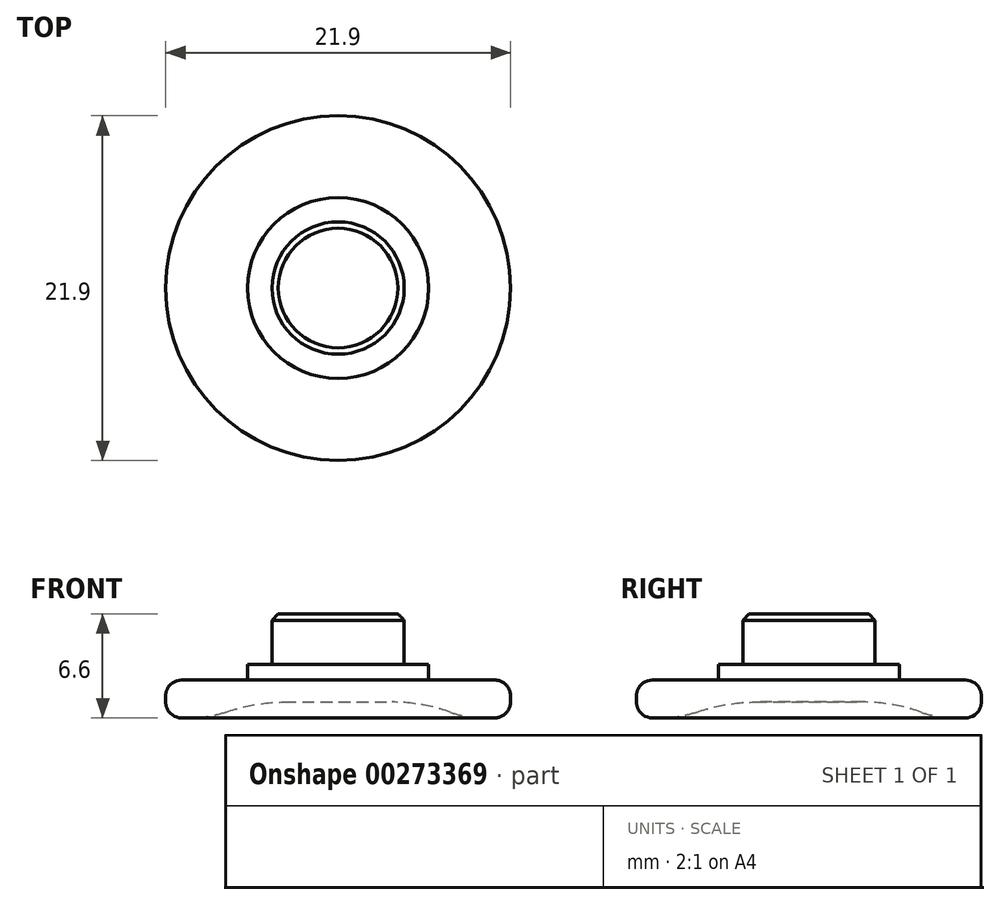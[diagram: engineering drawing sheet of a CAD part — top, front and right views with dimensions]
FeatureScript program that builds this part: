
annotation { "Feature Type Name" : "Feature", "Feature Type Description" : "" }
export const myFeature = defineFeature(function(context is Context, id is Id, definition is map)
    precondition{}
    {
        {
            var Q0;
            Q0=qCreatedBy(makeId("Top.planeOp"),FACE);
            var sketch = newSketch(context, id + "F0", { "sketchPlane" : qUnion([Q0])});
            skCircle(sketch, "E0", {"center": v(0, 0) * mm, "radius": 10.95 * mm});
            skSolve(sketch);
        }
        {
            var Q0;
            Q0=makeQuery(id+"F0.imprint","IMPRINT",FACE,{"disambiguationData":[TD([[makeQuery(id+"F0.imprint","IMPRINT",EDGE,{"derivedFrom":sQuery(id+"F0.wireOp",EDGE,"E0")}),1.0]])]});
            extrude(context, id + "F1", {"entities" : qUnion([Q0]), "depth" : 2.4 * mm});
        }
        {
            var Q0;
            Q0=makeQuery(id+"F1.opExtrude","CAP_FACE",FACE,{"disambiguationData":[OSD([sQuery(id+"F0.wireOp",EDGE,"E0")])],"isStart":false});
            var sketch = newSketch(context, id + "F2", { "sketchPlane" : qUnion([Q0])});
            skCircle(sketch, "E1", {"center": v(0, 0) * mm, "radius": 4.2 * mm});
            skSolve(sketch);
        }
        {
            var Q0;
            Q0=makeQuery(id+"F2.imprint","IMPRINT",FACE,{"disambiguationData":[TD([[makeQuery(id+"F2.imprint","IMPRINT",EDGE,{"derivedFrom":sQuery(id+"F2.wireOp",EDGE,"E1")}),1.0]])]});
            extrude(context, id + "F3", {"entities" : qUnion([Q0]), "operationType" : NewBodyOperationType.ADD, "depth" : 4.2 * mm});
        }
        {
            var Q0;
            Q0=makeQuery(id+"F1.opExtrude","CAP_EDGE",EDGE,{"disambiguationData":[OSD([sQuery(id+"F0.wireOp",EDGE,"E0")])],"isStart":false});
            fillet(context, id + "F4", {"entities" : qUnion([Q0]), "radius" : 1 * mm, "tangentPropagation" : true, "allowEdgeOverflow" : false});
        }
        {
            var Q0;
            Q0=makeQuery(id+"F1.opExtrude","CAP_FACE",FACE,{"disambiguationData":[OSD([sQuery(id+"F0.wireOp",EDGE,"E0")])],"isStart":false});
            var sketch = newSketch(context, id + "F5", { "sketchPlane" : qUnion([Q0])});
            skCircle(sketch, "E2", {"center": v(0, 0) * mm, "radius": 5.75 * mm});
            skSolve(sketch);
        }
        {
            var Q0;
            Q0=makeQuery(id+"F5.imprint","IMPRINT",FACE,{"disambiguationData":[TD([[makeQuery(id+"F5.imprint","IMPRINT",EDGE,{"derivedFrom":sQuery(id+"F5.wireOp",EDGE,"E2")}),1.0]])]});
            extrude(context, id + "F6", {"entities" : qUnion([Q0]), "operationType" : NewBodyOperationType.ADD, "depth" : 1 * mm});
        }
        {
            var Q0;
            Q0=makeQuery(id+"F1.opExtrude","CAP_EDGE",EDGE,{"disambiguationData":[OSD([sQuery(id+"F0.wireOp",EDGE,"E0")])],"isStart":true});
            fillet(context, id + "F7", {"entities" : qUnion([Q0]), "radius" : 1 * mm, "tangentPropagation" : true, "allowEdgeOverflow" : false});
        }
        {
            var Q0;
            Q0=makeQuery(id+"F1.opExtrude","CAP_FACE",FACE,{"disambiguationData":[OSD([sQuery(id+"F0.wireOp",EDGE,"E0")])],"isStart":true});
            var sketch = newSketch(context, id + "F8", { "sketchPlane" : qUnion([Q0])});
            skCircle(sketch, "E3", {"center": v(0, 0) * mm, "radius": 8 * mm});
            skSolve(sketch);
        }
        {
            var Q0;
            Q0=makeQuery(id+"F8.imprint","IMPRINT",FACE,{"disambiguationData":[TD([[makeQuery(id+"F8.imprint","IMPRINT",EDGE,{"derivedFrom":sQuery(id+"F8.wireOp",EDGE,"E3")}),1.0]])]});
            extrude(context, id + "F9", {"entities" : qUnion([Q0]), "operationType" : NewBodyOperationType.REMOVE, "oppositeDirection" : true, "depth" : 1 * mm});
        }
        {
            var Q0;
            Q0=makeQuery(id+"F9.boolean.opBoolean","COPY",EDGE,{"derivedFrom":makeQuery(id+"F9.opExtrude","CAP_EDGE",EDGE,{"disambiguationData":[OSD([sQuery(id+"F8.wireOp",EDGE,"E3")])],"isStart":false})});
            fillet(context, id + "F10", {"entities" : qUnion([Q0]), "radius" : 11 * mm, "tangentPropagation" : true, "allowEdgeOverflow" : false});
        }
        {
            var Q0;
            Q0=makeQuery(id+"F3.opExtrude","CAP_EDGE",EDGE,{"disambiguationData":[OSD([sQuery(id+"F2.wireOp",EDGE,"E1")])],"isStart":false});
            chamfer(context, id + "F11", {"entities" : qUnion([Q0]), "width" : .4 * mm, "tangentPropagation" : true});
        }
        {
            var Q0;
            Q0=makeQuery(id+"F10.opFillet","BLEND_EDGE",EDGE,{"blendedFrom":[makeQuery(id+"F9.boolean.opBoolean","COPY",EDGE,{"derivedFrom":makeQuery(id+"F9.opExtrude","CAP_EDGE",EDGE,{"disambiguationData":[OSD([sQuery(id+"F8.wireOp",EDGE,"E3")])],"isStart":false})}),makeQuery(id+"F1.opExtrude","CAP_FACE",FACE,{"disambiguationData":[OSD([sQuery(id+"F0.wireOp",EDGE,"E0")])],"isStart":true})],"blendedInto":[makeQuery(id+"F1.opExtrude","CAP_FACE",FACE,{"disambiguationData":[OSD([sQuery(id+"F0.wireOp",EDGE,"E0")])],"isStart":true})]});
            fillet(context, id + "F12", {"entities" : qUnion([Q0]), "radius" : 6 * mm, "tangentPropagation" : true, "allowEdgeOverflow" : false});
        }
    });
